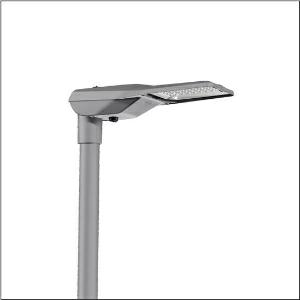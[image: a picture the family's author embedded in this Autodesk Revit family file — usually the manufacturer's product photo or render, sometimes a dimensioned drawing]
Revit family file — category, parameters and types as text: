
# Revit family: streetlight_sl_21_iq_mini___st1_5a_5xe2p31y08hb_ad09
name_source: partatom
category: Lighting Fixtures
units: mm (PartAtom-declared; Revit-internal decimal feet)

## family parameters
Cut with Voids When Loaded = No
Host = Face
Light Source = No
Part Type = Normal
Room Calculation Point = No
Round Connector Dimension = Use Diameter
Shared = No

## types (1)
- --- (1 x LED, 9580 lm, 71 W, 3000K)
    Apparent Load = 71 VA
    CIE Flux Codes = 22 53 95 100 100
    Color Rendering = 70
    Color Temperature = 3000K
    Default Elevation = 1800 mm
    Description = Streetlight SL 21 iQ mini, mast luminaire, primary light control with lens, of PMMA, primary optical cover: cover, of toughened safety glass, transparent, light distribution: ST1.5a, light emission: direct distribution, primary light characteristic: asymmetric, installation type: post-top, side-entry, LED, High Power LED, rated luminous flux: 9.580lm, luminous efficacy: 135lm/W, light colour: 730, colour temperature: 3000K, control: presetting dimming logarithmic, Street-Remote, Auto-Match, Temp-Guard, Lumen-Switch, Night-Set, Smart-Wire, Light-Fading, Desk-Remote (wireless, voltage-free reading and setting of iQ features in the workshop via application-optimized NFC function/RFID function), optimised constant luminous flux control (CLO 2.0), mains connection: 220..240V, AC, 50/60Hz, start of lifetime: 71W, end of service life: 75W, reduction: 30W, luminaire housing, of diecast aluminium, powder-coated, Siteco® metallic grey (DB 702S), corrosivity category C5 mid according to DIN EN ISO 12944, please order mast flange separately, inclination adjustable: 0°, 5°, 10°, 15°, sealing non-destructively replaceable, multi-level sealing system, length: 628mm, width: 235mm, height: 110mm, mast flange for spigot size: 42mm (side-entry): 5XC10008XM4, 60/48mm (side-entry/post-top): 5XC10108XM2, 76/60mm (side-entry/post-top): 5XC10108XM1, Smart Interface below and above, protection rating (complete): IP66, insulation class (complete): insulation class II (safety insulation), certification: CE, ENEC, ENEC+, VDE, impact resistance: IK09, permissible operating ambient temperature for outdoor applications: -40..+50°C, standard-compliant lighting for roads and squares, packaging unit: 1 piece

Light Distribution: ST1.5a
    Height = 110 mm
    Lamp = 1 x LED
    Lamp Light Flux = 9580 lm
    Lamp Power = 71 W
    Lamp count = 1
    Length = 625 mm
    Luminous efficacy = 135 lm/W
    Manufacturer = Siteco
    ModVariant = No
    Model = 5XE2P31Y08HB
    Number of Poles = 1
    OnlyDefault = Yes
    Power Factor = 1
    Product Name = Streetlight SL 21 iQ mini | ST1.5a
    Product group = mast luminaire | pylon top
    ProductGroupID = 6100
    Protection Class = Protection class II
    Protection Degree = IP 66
    RLX_Detail_Level = 1
    RLX_Emergency_Light_Flux = 0 lm
    RLX_Emergency_Type = 0
    RLX_Emergency_Type_DB = No
    RlxData = <blob elided: 95965 chars, md5=65b54850>
    Socket = socket
    Standby Power = 0 W
    System Light Flux = 9580 lm
    System Power = 71 W
    Type Comments = factory setting: luminous flux: 100 % | dim-lin: 254 | 716 mA
    Type Image = l_1003514.jpg
    URL = http://relux.com
    VarID = @adj_060145
    Voltage = 0 V
    Weight = 0.00 kg
    Width = 234 mm

## geometry (parser evidence)
native form markers: Blend x4, Sweep x10
no freeform markers — native parametric forms only
